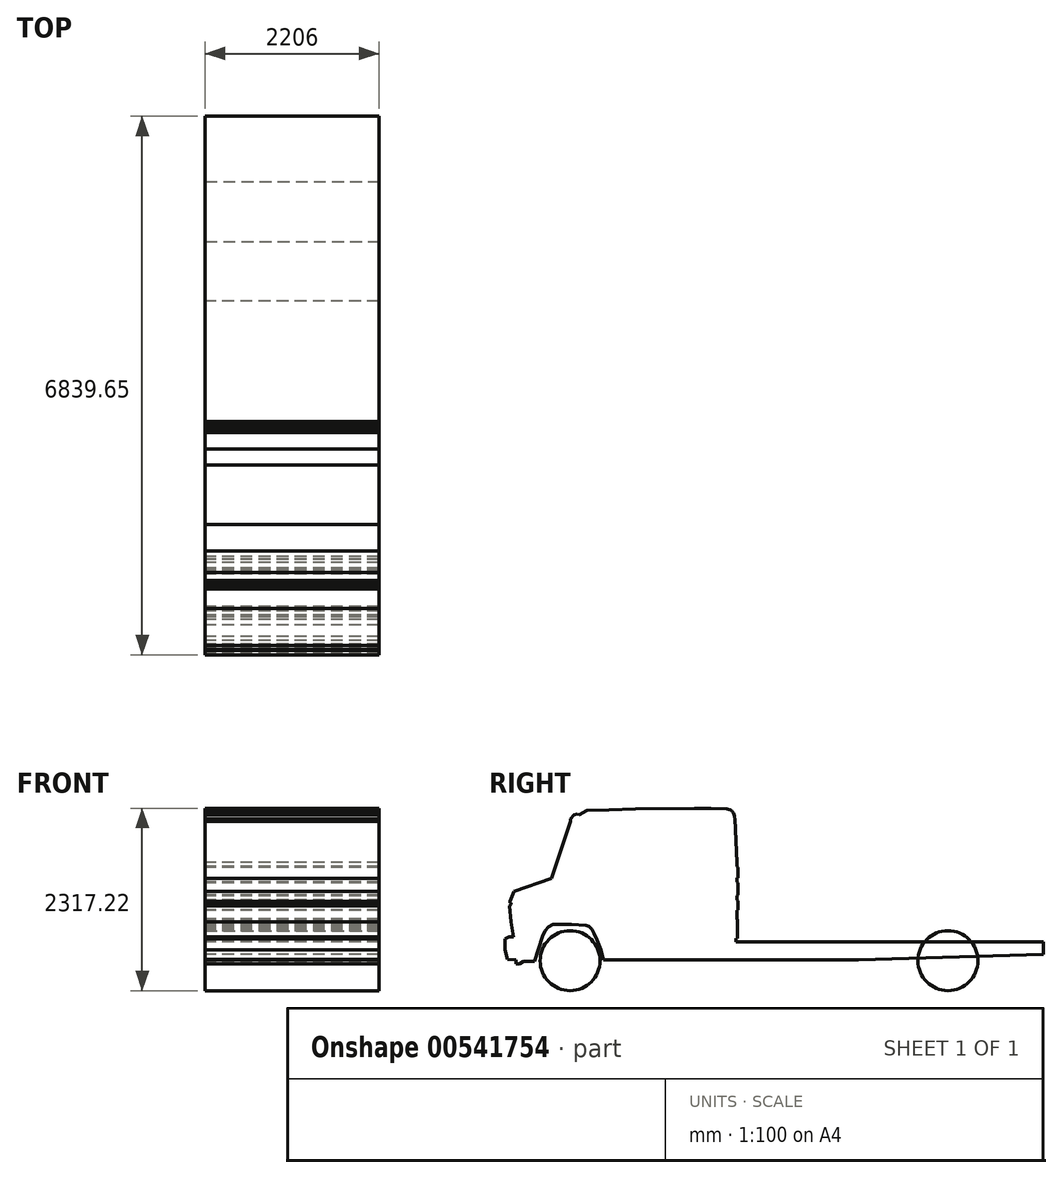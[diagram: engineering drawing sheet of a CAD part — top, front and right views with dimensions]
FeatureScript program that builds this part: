
annotation { "Feature Type Name" : "Feature", "Feature Type Description" : "" }
export const myFeature = defineFeature(function(context is Context, id is Id, definition is map)
    precondition{}
    {
        {
            var Q0;
            Q0=qCreatedBy(makeId("Right.planeOp"),FACE);
            var sketch = newSketch(context, id + "F0", { "sketchPlane" : qUnion([Q0])});
            skLineSegment(sketch, "E0", {"start": v(-42.86, 852.32) * mm, "end": v(-42.86, -853.68) * mm, "construction": true});
            skLineSegment(sketch, "E1", {"start": v(-1974.88, -795.3) * mm, "end": v(-2009.8, -605.71) * mm});
            skLineSegment(sketch, "E2", {"start": v(-2009.8, -605.71) * mm, "end": v(-2029.02, -400.75) * mm});
            skLineSegment(sketch, "E3", {"start": v(-2029.02, -400.75) * mm, "end": v(-2009.8, -385.39) * mm});
            skLineSegment(sketch, "E4", {"start": v(-2009.8, -385.39) * mm, "end": v(-2009.8, -366.18) * mm});
            skLineSegment(sketch, "E5", {"start": v(-2009.8, -366.18) * mm, "end": v(-2021.33, -366.18) * mm});
            skLineSegment(sketch, "E6", {"start": v(-2021.33, -366.18) * mm, "end": v(-2021.33, -346.97) * mm});
            skLineSegment(sketch, "E7", {"start": v(-2021.33, -346.97) * mm, "end": v(-1970.86, -215.74) * mm});
            skLineSegment(sketch, "E8", {"start": v(-1970.86, -215.74) * mm, "end": v(-1496.42, -54.23) * mm});
            skLineSegment(sketch, "E9", {"start": v(-1496.42, -54.23) * mm, "end": v(-1252.7, 673.97) * mm});
            skLineSegment(sketch, "E10", {"start": v(-1252.7, 673.97) * mm, "end": v(-1252.7, 705.7) * mm});
            skLineSegment(sketch, "E11", {"start": v(-1252.7, 705.7) * mm, "end": v(-1208.75, 752.1) * mm});
            skLineSegment(sketch, "E12", {"start": v(-1208.75, 752.1) * mm, "end": v(-1162.37, 766.74) * mm});
            skLineSegment(sketch, "E13", {"start": v(-1162.37, 766.74) * mm, "end": v(-1142.84, 756.97) * mm});
            skLineSegment(sketch, "E14", {"start": v(-1142.84, 756.97) * mm, "end": v(-1042.41, 812.77) * mm});
            skLineSegment(sketch, "E15", {"start": v(-1042.41, 812.77) * mm, "end": v(-766.9, 815.56) * mm});
            skLineSegment(sketch, "E16", {"start": v(-766.9, 815.56) * mm, "end": v(-429.07, 828.35) * mm});
            skLineSegment(sketch, "E17", {"start": v(-429.07, 828.35) * mm, "end": v(321.31, 838.73) * mm});
            skLineSegment(sketch, "E18", {"start": v(321.31, 838.73) * mm, "end": v(528.45, 838.73) * mm});
            skLineSegment(sketch, "E19", {"start": v(528.45, 838.73) * mm, "end": v(733.47, 828.35) * mm});
            skLineSegment(sketch, "E20", {"start": v(733.47, 828.35) * mm, "end": v(754.7, 826) * mm});
            skLineSegment(sketch, "E21", {"start": v(754.7, 826) * mm, "end": v(780.64, 815.56) * mm});
            skLineSegment(sketch, "E22", {"start": v(780.64, 815.56) * mm, "end": v(794.07, 806.34) * mm});
            skLineSegment(sketch, "E23", {"start": v(794.07, 806.34) * mm, "end": v(805.18, 795.2) * mm});
            skLineSegment(sketch, "E24", {"start": v(805.18, 795.2) * mm, "end": v(814.91, 778.83) * mm});
            skLineSegment(sketch, "E25", {"start": v(814.91, 778.83) * mm, "end": v(821.87, 762.49) * mm});
            skLineSegment(sketch, "E26", {"start": v(821.87, 762.49) * mm, "end": v(826.54, 743.26) * mm});
            skLineSegment(sketch, "E27", {"start": v(826.54, 743.26) * mm, "end": v(835.04, 691.6) * mm});
            skLineSegment(sketch, "E28", {"start": v(835.04, 691.6) * mm, "end": v(837.59, 677.8) * mm});
            skLineSegment(sketch, "E29", {"start": v(837.3, 705.2) * mm, "end": v(837.59, 677.8) * mm});
            skLineSegment(sketch, "E30", {"start": v(837.3, 705.2) * mm, "end": v(863.14, 151.63) * mm});
            skLineSegment(sketch, "E31", {"start": v(863.14, 151.63) * mm, "end": v(863.14, 136.11) * mm});
            skLineSegment(sketch, "E32", {"start": v(863.14, 136.11) * mm, "end": v(863.14, 97.3) * mm});
            skLineSegment(sketch, "E33", {"start": v(863.14, 97.3) * mm, "end": v(872.27, 88.16) * mm});
            skLineSegment(sketch, "E34", {"start": v(872.27, 88.16) * mm, "end": v(872.27, -46.28) * mm});
            skLineSegment(sketch, "E35", {"start": v(872.27, -46.28) * mm, "end": v(863.14, -46.28) * mm});
            skLineSegment(sketch, "E36", {"start": v(863.14, -46.28) * mm, "end": v(863.67, -97.85) * mm});
            skLineSegment(sketch, "E37", {"start": v(863.67, -97.85) * mm, "end": v(873.98, -109.18) * mm});
            skLineSegment(sketch, "E38", {"start": v(873.98, -109.18) * mm, "end": v(873.98, -263.08) * mm});
            skLineSegment(sketch, "E39", {"start": v(873.98, -263.08) * mm, "end": v(863.67, -274.42) * mm});
            skLineSegment(sketch, "E40", {"start": v(863.67, -274.42) * mm, "end": v(863.67, -325.08) * mm});
            skLineSegment(sketch, "E41", {"start": v(863.67, -325.08) * mm, "end": v(875.77, -336.85) * mm});
            skLineSegment(sketch, "E42", {"start": v(875.77, -336.85) * mm, "end": v(875.77, -451.97) * mm});
            skLineSegment(sketch, "E43", {"start": v(875.77, -451.97) * mm, "end": v(863.67, -459.6) * mm});
            skLineSegment(sketch, "E44", {"start": v(863.67, -459.6) * mm, "end": v(863.67, -565.83) * mm});
            skLineSegment(sketch, "E45", {"start": v(863.67, -565.83) * mm, "end": v(870.28, -576.9) * mm});
            skLineSegment(sketch, "E46", {"start": v(870.28, -576.9) * mm, "end": v(870.28, -812.06) * mm});
            skLineSegment(sketch, "E47", {"start": v(870.28, -812.06) * mm, "end": v(850.13, -812.06) * mm});
            skLineSegment(sketch, "E48", {"start": v(850.13, -812.06) * mm, "end": v(850.13, -858.33) * mm});
            skLineSegment(sketch, "E49", {"start": v(850.13, -858.33) * mm, "end": v(4752.7, -858.33) * mm});
            skLineSegment(sketch, "E50", {"start": v(4752.7, -858.33) * mm, "end": v(4752.7, -1018.39) * mm});
            skLineSegment(sketch, "E51", {"start": v(4752.7, -1018.39) * mm, "end": v(2405.63, -1088.75) * mm});
            skLineSegment(sketch, "E52", {"start": v(2405.63, -1088.75) * mm, "end": v(-848.53, -1088.75) * mm});
            skLineSegment(sketch, "E53", {"start": v(-1852.5, -1104.3) * mm, "end": v(-1903.14, -1139.96) * mm});
            skLineSegment(sketch, "E54", {"start": v(-1903.14, -1139.96) * mm, "end": v(-1948.16, -1139.96) * mm});
            skLineSegment(sketch, "E55", {"start": v(-1948.16, -1139.96) * mm, "end": v(-1948.16, -1088.75) * mm});
            skLineSegment(sketch, "E56", {"start": v(-1948.16, -1088.75) * mm, "end": v(-2055.07, -1078.06) * mm});
            skLineSegment(sketch, "E57", {"start": v(-2055.07, -1078.06) * mm, "end": v(-2086.95, -963.02) * mm});
            skLineSegment(sketch, "E58", {"start": v(-2086.95, -963.02) * mm, "end": v(-2086.95, -822) * mm});
            skLineSegment(sketch, "E59", {"start": v(-2086.95, -822) * mm, "end": v(-2034.07, -792.6) * mm});
            skLineSegment(sketch, "E60", {"start": v(-2034.07, -792.6) * mm, "end": v(-1974.88, -795.3) * mm});
            skLineSegment(sketch, "E61", {"start": v(-1708.53, -1104.3) * mm, "end": v(-1609.16, -788.35) * mm});
            skLineSegment(sketch, "E62", {"start": v(-1609.16, -788.35) * mm, "end": v(-1580.77, -722.1) * mm});
            skLineSegment(sketch, "E63", {"start": v(-1580.77, -722.1) * mm, "end": v(-1533.45, -665.32) * mm});
            skLineSegment(sketch, "E64", {"start": v(-1533.45, -665.32) * mm, "end": v(-1476.67, -636.93) * mm});
            skLineSegment(sketch, "E65", {"start": v(-1476.67, -636.93) * mm, "end": v(-1419.88, -636.93) * mm});
            skLineSegment(sketch, "E66", {"start": v(-1419.88, -636.93) * mm, "end": v(-1240.07, -636.93) * mm});
            skLineSegment(sketch, "E67", {"start": v(-1240.07, -636.93) * mm, "end": v(-1057.89, -648.76) * mm});
            skLineSegment(sketch, "E68", {"start": v(-1057.89, -648.76) * mm, "end": v(-1036.14, -654.14) * mm});
            skLineSegment(sketch, "E69", {"start": v(-1036.14, -654.14) * mm, "end": v(-1019.37, -663.17) * mm});
            skLineSegment(sketch, "E70", {"start": v(-1019.37, -663.17) * mm, "end": v(-998.73, -681.23) * mm});
            skLineSegment(sketch, "E71", {"start": v(-998.73, -681.23) * mm, "end": v(-983.25, -701.87) * mm});
            skLineSegment(sketch, "E72", {"start": v(-983.25, -701.87) * mm, "end": v(-957.45, -750.89) * mm});
            skLineSegment(sketch, "E73", {"start": v(-957.45, -750.89) * mm, "end": v(-914.88, -833.45) * mm});
            skLineSegment(sketch, "E74", {"start": v(-914.88, -833.45) * mm, "end": v(-869.72, -957.3) * mm});
            skLineSegment(sketch, "E75", {"start": v(-869.72, -957.3) * mm, "end": v(-837.7, -1088.75) * mm});
            skLineSegment(sketch, "E76", {"start": v(-1852.5, -1104.3) * mm, "end": v(-1708.53, -1104.3) * mm});
            skCircle(sketch, "E77", {"center": v(-1259.2, -1097.97) * mm, "radius": 380.52 * mm});
            skSolve(sketch);
        }
        {
            var Q0;
            Q0=makeQuery(id+"F0.imprint","IMPRINT",FACE,{"disambiguationData":[TD([[makeQuery(id+"F0.imprint","IMPRINT",EDGE,{"derivedFrom":sQuery(id+"F0.wireOp",EDGE,"E1")}),-1.0]])]});
            extrude(context, id + "F1", {"entities" : qUnion([Q0]), "depth" : 2206 * mm, "offsetDistance" : 25 * mm});
        }
        {
            var Q0;
            Q0 = qSketchRegion(id + "F0", true);
            extrude(context, id + "F2", {"entities" : qUnion([Q0]), "operationType" : NewBodyOperationType.ADD, "depth" : 2206 * mm, "offsetDistance" : 25 * mm});
        }
        {
            var Q0;
            Q0=makeQuery(id+"F1.opExtrude","CAP_FACE",FACE,{"disambiguationData":[OSD([sQuery(id+"F0.wireOp",EDGE,"E1"),sQuery(id+"F0.wireOp",EDGE,"E2"),sQuery(id+"F0.wireOp",EDGE,"E3"),sQuery(id+"F0.wireOp",EDGE,"E4"),sQuery(id+"F0.wireOp",EDGE,"E5"),sQuery(id+"F0.wireOp",EDGE,"E6"),sQuery(id+"F0.wireOp",EDGE,"E7"),sQuery(id+"F0.wireOp",EDGE,"E8"),sQuery(id+"F0.wireOp",EDGE,"E9"),sQuery(id+"F0.wireOp",EDGE,"E10"),sQuery(id+"F0.wireOp",EDGE,"E11"),sQuery(id+"F0.wireOp",EDGE,"E12"),sQuery(id+"F0.wireOp",EDGE,"E13"),sQuery(id+"F0.wireOp",EDGE,"E14"),sQuery(id+"F0.wireOp",EDGE,"E15"),sQuery(id+"F0.wireOp",EDGE,"E16"),sQuery(id+"F0.wireOp",EDGE,"E17"),sQuery(id+"F0.wireOp",EDGE,"E18"),sQuery(id+"F0.wireOp",EDGE,"E19"),sQuery(id+"F0.wireOp",EDGE,"E20"),sQuery(id+"F0.wireOp",EDGE,"E21"),sQuery(id+"F0.wireOp",EDGE,"E22"),sQuery(id+"F0.wireOp",EDGE,"E23"),sQuery(id+"F0.wireOp",EDGE,"E24"),sQuery(id+"F0.wireOp",EDGE,"E25"),sQuery(id+"F0.wireOp",EDGE,"E26"),sQuery(id+"F0.wireOp",EDGE,"E27"),sQuery(id+"F0.wireOp",EDGE,"E28"),sQuery(id+"F0.wireOp",EDGE,"E29"),sQuery(id+"F0.wireOp",EDGE,"E30"),sQuery(id+"F0.wireOp",EDGE,"E31"),sQuery(id+"F0.wireOp",EDGE,"E32"),sQuery(id+"F0.wireOp",EDGE,"E33"),sQuery(id+"F0.wireOp",EDGE,"E34"),sQuery(id+"F0.wireOp",EDGE,"E35"),sQuery(id+"F0.wireOp",EDGE,"E36"),sQuery(id+"F0.wireOp",EDGE,"E37"),sQuery(id+"F0.wireOp",EDGE,"E38"),sQuery(id+"F0.wireOp",EDGE,"E39"),sQuery(id+"F0.wireOp",EDGE,"E40"),sQuery(id+"F0.wireOp",EDGE,"E41"),sQuery(id+"F0.wireOp",EDGE,"E42"),sQuery(id+"F0.wireOp",EDGE,"E43"),sQuery(id+"F0.wireOp",EDGE,"E44"),sQuery(id+"F0.wireOp",EDGE,"E45"),sQuery(id+"F0.wireOp",EDGE,"E46"),sQuery(id+"F0.wireOp",EDGE,"E47"),sQuery(id+"F0.wireOp",EDGE,"E48"),sQuery(id+"F0.wireOp",EDGE,"E49"),sQuery(id+"F0.wireOp",EDGE,"E50"),sQuery(id+"F0.wireOp",EDGE,"E51"),sQuery(id+"F0.wireOp",EDGE,"E52"),sQuery(id+"F0.wireOp",EDGE,"E53"),sQuery(id+"F0.wireOp",EDGE,"E54"),sQuery(id+"F0.wireOp",EDGE,"E55"),sQuery(id+"F0.wireOp",EDGE,"E56"),sQuery(id+"F0.wireOp",EDGE,"E57"),sQuery(id+"F0.wireOp",EDGE,"E58"),sQuery(id+"F0.wireOp",EDGE,"E59"),sQuery(id+"F0.wireOp",EDGE,"E60"),sQuery(id+"F0.wireOp",EDGE,"E61"),sQuery(id+"F0.wireOp",EDGE,"E62"),sQuery(id+"F0.wireOp",EDGE,"E63"),sQuery(id+"F0.wireOp",EDGE,"E64"),sQuery(id+"F0.wireOp",EDGE,"E65"),sQuery(id+"F0.wireOp",EDGE,"E66"),sQuery(id+"F0.wireOp",EDGE,"E67"),sQuery(id+"F0.wireOp",EDGE,"E68"),sQuery(id+"F0.wireOp",EDGE,"E69"),sQuery(id+"F0.wireOp",EDGE,"E70"),sQuery(id+"F0.wireOp",EDGE,"E71"),sQuery(id+"F0.wireOp",EDGE,"E72"),sQuery(id+"F0.wireOp",EDGE,"E73"),sQuery(id+"F0.wireOp",EDGE,"E74"),sQuery(id+"F0.wireOp",EDGE,"E75"),sQuery(id+"F0.wireOp",EDGE,"E76")])],"isStart":false});
            var sketch = newSketch(context, id + "F3", { "sketchPlane" : qUnion([Q0])});
            skCircle(sketch, "E78", {"center": v(3540.8, -1097.97) * mm, "radius": 380.5 * mm});
            skLineSegment(sketch, "E79", {"start": v(-1259.2, -1097.97) * mm, "end": v(3540.8, -1097.97) * mm});
            skSolve(sketch);
        }
        {
            var Q0;
            {var subQ0=sQuery(id+"F3.wireOp",EDGE,"E78");var subQ1=makeQuery(id+"F1.opExtrude","CAP_EDGE",EDGE,{"disambiguationData":[OSD([sQuery(id+"F0.wireOp",EDGE,"E49")])],"isStart":false});var subQ2=makeQuery(id+"F3.imprint","INTERSECT",VERTEX,{"disambiguationData":[OD(0.0)],"derivedFrom":[subQ1,subQ0]});Q0=makeQuery(id+"F3.imprint","IMPRINT",FACE,{"disambiguationData":[TD([[makeQuery(id+"F3.imprint","IMPRINT",EDGE,{"disambiguationData":[TD([[subQ2,-1.0]])],"derivedFrom":subQ0}),1.0]])]});}
            var Q1;
            {var subQ0=sQuery(id+"F3.wireOp",EDGE,"E78");var subQ1=makeQuery(id+"F1.opExtrude","CAP_EDGE",EDGE,{"disambiguationData":[OSD([sQuery(id+"F0.wireOp",EDGE,"E49")])],"isStart":false});var subQ2=makeQuery(id+"F3.imprint","INTERSECT",VERTEX,{"disambiguationData":[OD(0.0)],"derivedFrom":[subQ1,subQ0]});Q1=makeQuery(id+"F3.imprint","IMPRINT",FACE,{"disambiguationData":[TD([[makeQuery(id+"F3.imprint","IMPRINT",EDGE,{"disambiguationData":[TD([[subQ2,1.0]])],"derivedFrom":subQ0}),1.0]])]});}
            var Q2;
            {var subQ0=sQuery(id+"F3.wireOp",EDGE,"E78");var subQ1=makeQuery(id+"F1.opExtrude","CAP_EDGE",EDGE,{"disambiguationData":[OSD([sQuery(id+"F0.wireOp",EDGE,"E51")])],"isStart":false});var subQ2=makeQuery(id+"F3.imprint","INTERSECT",VERTEX,{"disambiguationData":[OD(0.0)],"derivedFrom":[subQ1,subQ0]});Q2=makeQuery(id+"F3.imprint","IMPRINT",FACE,{"disambiguationData":[TD([[makeQuery(id+"F3.imprint","IMPRINT",EDGE,{"disambiguationData":[TD([[subQ2,1.0]])],"derivedFrom":subQ0}),1.0]])]});}
            extrude(context, id + "F4", {"entities" : qUnion([Q0, Q1, Q2]), "oppositeDirection" : true, "depth" : 2206 * mm, "offsetDistance" : 25 * mm});
        }
    });
